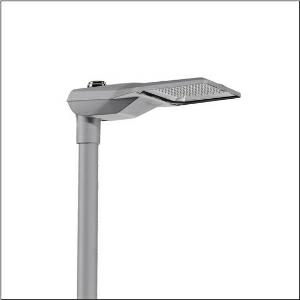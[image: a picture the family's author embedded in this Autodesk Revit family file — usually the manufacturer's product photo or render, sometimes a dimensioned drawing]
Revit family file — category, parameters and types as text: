
# Revit family: streetlight_sl_21_midi___p0_8a_5xe7u67n08lb_2465
name_source: partatom
category: Lighting Fixtures
units: mm (PartAtom-declared; Revit-internal decimal feet)

## family parameters
Cut with Voids When Loaded = No
Host = Face
Light Source = No
Part Type = Normal
Room Calculation Point = No
Round Connector Dimension = Use Diameter
Shared = No

## types (1)
- --- (1 x LED, 12970 lm, 98.3 W, 2700K)
    Apparent Load = 98 VA
    CIE Flux Codes = 33 69 96 100 100
    Color Rendering = 70
    Color Temperature = 2700K
    Default Elevation = 1800 mm
    Description = Streetlight SL 21 midi, mast luminaire, primary light control with lens, of PMMA, primary optical cover: cover, of toughened safety glass, transparent, light distribution: P0.8a, light emission: direct distribution, primary light characteristic: asymmetric, installation type: side-entry, LED, 3G 2.5mm², High Power LED, rated luminous flux: 12.970lm, luminous efficacy: 132lm/W, light colour: 727, colour temperature: 2700K, control gear: NEMA (7pin), control: flexible luminous flux parameterisation, time-dependent luminous flux control, constant luminous flux control, pre-setting: linear dimming characteristic, overheat protection, mains connection: 220..240V, AC, 50/60Hz, connection cable pre-assembled, cable length: 10,5m, wiring characteristics: H05VV-F, start of lifetime: 98W, end of service life: 101W, reduction: 45W, luminaire housing, of diecast aluminium (EN AC-44300), powder-coated, Siteco® metallic grey (DB 702S), corrosivity category C5 mid according to DIN EN ISO 12944, multi-level sealing system, sealing non-destructively replaceable, inclination adjustable: 0°, 5°, 10°, 15°, length: 644mm, width: 335mm, height: 110mm, spigot size: 42mm (side-entry), mounting height: 4..8m, protection rating (complete): IP66, insulation class (complete): insulation class I (protective earthing), certification: CE, ENEC, ENEC+, VDE, impact resistance: IK10, permissible operating ambient temperature for outdoor applications: -40..+50°C, standard-compliant lighting for roads and squares, packaging unit: 1 piece

Light Distribution: P0.8a
    Height = 111 mm
    Lamp = 1 x LED
    Lamp Light Flux = 12970 lm
    Lamp Power = 98.3 W
    Lamp count = 1
    Length = 644 mm
    Luminous efficacy = 132 lm/W
    Manufacturer = Siteco
    ModVariant = No
    Model = 5XE7U67N08LB
    Number of Poles = 1
    OnlyDefault = Yes
    Power Factor = 1
    Product Name = Streetlight SL 21 midi | P0.8a
    Product group = mast luminaire | pylon top
    ProductGroupID = 6100
    Protection Class = Protection class I
    Protection Degree = IP 66
    RLX_Detail_Level = 1
    RLX_Emergency_Light_Flux = 0 lm
    RLX_Emergency_Type = 0
    RLX_Emergency_Type_DB = No
    RlxData = <blob elided: 26413 chars, md5=1a4f9d88>
    Socket = socket
    Standby Power = 0 W
    System Light Flux = 12970 lm
    System Power = 98 W
    Type Comments = factory setting: luminous flux: 100 % | dim-lin: 254 | 1020 mA
    Type Image = l_1294377.jpg
    URL = http://relux.com
    VarID = @adj_073190
    Voltage = 0 V
    Weight = 0.00 kg
    Width = 336 mm

## geometry (parser evidence)
native form markers: Blend x4, Sweep x13
no freeform markers — native parametric forms only
